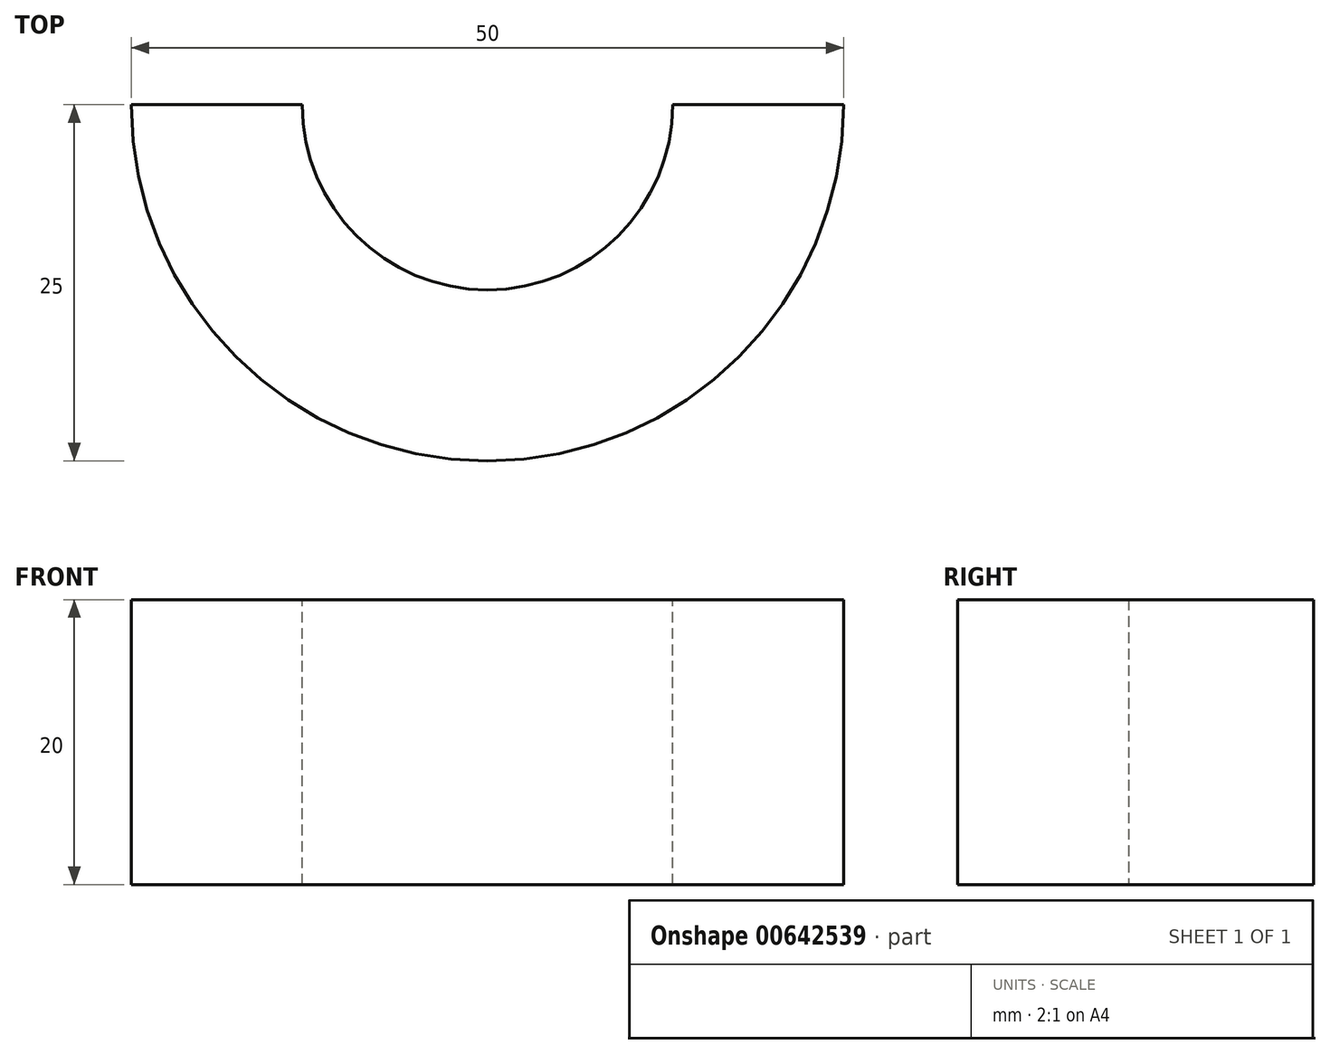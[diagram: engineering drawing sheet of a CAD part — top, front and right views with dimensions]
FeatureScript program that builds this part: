
annotation { "Feature Type Name" : "Feature", "Feature Type Description" : "" }
export const myFeature = defineFeature(function(context is Context, id is Id, definition is map)
    precondition{}
    {
        {
            var Q0;
            Q0=qCreatedBy(makeId("Front.planeOp"),FACE);
            var sketch = newSketch(context, id + "F0", { "sketchPlane" : qUnion([Q0])});
            skLineSegment(sketch, "E0.right", {"start": v(-32.04, 9.77) * mm, "end": v(-32.04, 29.77) * mm});
            skLineSegment(sketch, "E1", {"start": v(17.96, 9.77) * mm, "end": v(17.96, 29.77) * mm});
            skLineSegment(sketch, "E2", {"start": v(-20.04, 9.77) * mm, "end": v(-20.04, 29.77) * mm});
            skLineSegment(sketch, "E3", {"start": v(5.96, 29.77) * mm, "end": v(5.96, 9.77) * mm});
            skLineSegment(sketch, "E4", {"start": v(5.96, 29.77) * mm, "end": v(17.96, 29.77) * mm});
            skLineSegment(sketch, "E5", {"start": v(-32.04, 29.77) * mm, "end": v(-20.04, 29.77) * mm});
            skLineSegment(sketch, "E6", {"start": v(-32.04, 9.77) * mm, "end": v(-20.04, 9.77) * mm});
            skLineSegment(sketch, "E7", {"start": v(5.96, 9.77) * mm, "end": v(17.96, 9.77) * mm});
            skLineSegment(sketch, "E8", {"start": v(-7.04, 9.77) * mm, "end": v(-7.04, 29.9) * mm});
            skSolve(sketch);
        }
        {
            var Q0;
            Q0=makeQuery(id+"F0.imprint","IMPRINT",FACE,{"disambiguationData":[TD([[makeQuery(id+"F0.imprint","IMPRINT",EDGE,{"derivedFrom":sQuery(id+"F0.wireOp",EDGE,"E0.right")}),-1.0]])]});
            var Q1;
            Q1=sQuery(id+"F0.wireOp",EDGE,"E8");
            revolve(context, id + "F1", {"entities" : qUnion([Q0]), "axis" : qUnion([Q1]), "revolveType" : RevolveType.ONE_DIRECTION, "angle" : 180 * degree});
        }
    });
